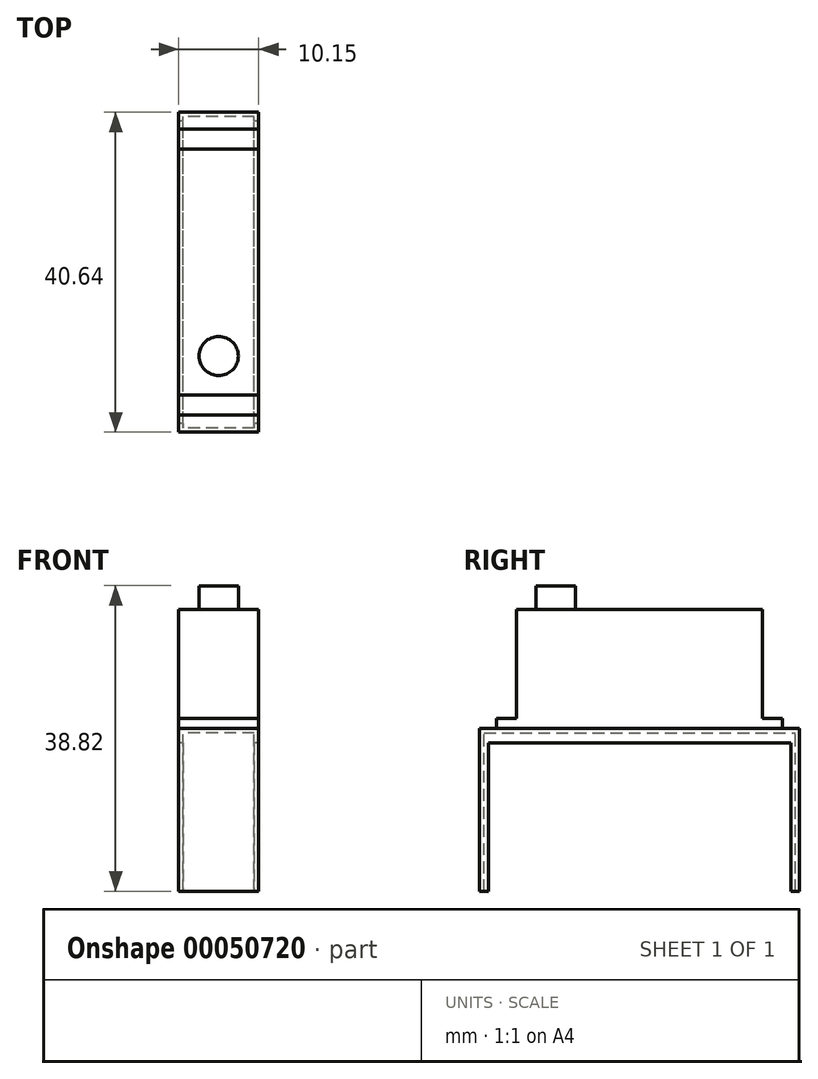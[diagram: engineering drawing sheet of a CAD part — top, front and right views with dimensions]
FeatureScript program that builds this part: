
annotation { "Feature Type Name" : "Feature", "Feature Type Description" : "" }
export const myFeature = defineFeature(function(context is Context, id is Id, definition is map)
    precondition{}
    {
        {
            var Q0;
            Q0=qCreatedBy(makeId("Top.planeOp"),FACE);
            var sketch = newSketch(context, id + "F0", { "sketchPlane" : qUnion([Q0])});
            skLineSegment(sketch, "E0", {"start": v(-5.08, -15.62) * mm, "end": v(-5.08, 15.61) * mm});
            skLineSegment(sketch, "E1", {"start": v(5.07, 15.61) * mm, "end": v(5.07, -15.62) * mm});
            skLineSegment(sketch, "E2", {"start": v(5.07, 15.61) * mm, "end": v(-5.08, 15.61) * mm});
            skLineSegment(sketch, "E3", {"start": v(-5.08, -15.62) * mm, "end": v(5.07, -15.62) * mm});
            skLineSegment(sketch, "E4", {"start": v(-5.08, 15.61) * mm, "end": v(-5.08, 18.17) * mm});
            skLineSegment(sketch, "E5", {"start": v(-5.08, 18.17) * mm, "end": v(5.07, 18.17) * mm});
            skLineSegment(sketch, "E6", {"start": v(5.07, 18.17) * mm, "end": v(5.07, 15.61) * mm});
            skLineSegment(sketch, "E7", {"start": v(-5.08, -15.62) * mm, "end": v(-5.08, -18.16) * mm});
            skLineSegment(sketch, "E8", {"start": v(-5.08, -18.16) * mm, "end": v(5.07, -18.16) * mm});
            skLineSegment(sketch, "E9", {"start": v(5.07, -18.16) * mm, "end": v(5.07, -15.62) * mm});
            skSolve(sketch);
        }
        {
            var Q0;
            Q0=makeQuery(id+"F0.imprint","IMPRINT",FACE,{"disambiguationData":[TD([[makeQuery(id+"F0.imprint","IMPRINT",EDGE,{"derivedFrom":sQuery(id+"F0.wireOp",EDGE,"E0")}),-1.0]])]});
            extrude(context, id + "F1", {"entities" : qUnion([Q0]), "depth" : 15.1 * mm});
        }
        {
            var Q0;
            Q0=makeQuery(id+"F0.imprint","IMPRINT",FACE,{"disambiguationData":[TD([[makeQuery(id+"F0.imprint","IMPRINT",EDGE,{"derivedFrom":sQuery(id+"F0.wireOp",EDGE,"E3")}),-1.0]])]});
            var Q1;
            Q1=makeQuery(id+"F0.imprint","IMPRINT",FACE,{"disambiguationData":[TD([[makeQuery(id+"F0.imprint","IMPRINT",EDGE,{"derivedFrom":sQuery(id+"F0.wireOp",EDGE,"E2")}),-1.0]])]});
            extrude(context, id + "F2", {"entities" : qUnion([Q0, Q1]), "operationType" : NewBodyOperationType.ADD, "depth" : 1.27 * mm});
        }
        {
            var Q0;
            Q0=makeQuery(id+"F1.opExtrude","CAP_FACE",FACE,{"disambiguationData":[OSD([sQuery(id+"F0.wireOp",EDGE,"E0"),sQuery(id+"F0.wireOp",EDGE,"E1"),sQuery(id+"F0.wireOp",EDGE,"E2"),sQuery(id+"F0.wireOp",EDGE,"E3")])],"isStart":false});
            var sketch = newSketch(context, id + "F3", { "sketchPlane" : qUnion([Q0])});
            skCircle(sketch, "E10", {"center": v(0, -10.64) * mm, "radius": 2.49 * mm});
            skSolve(sketch);
        }
        {
            var Q0;
            Q0=makeQuery(id+"F3.imprint","IMPRINT",FACE,{"disambiguationData":[TD([[makeQuery(id+"F3.imprint","IMPRINT",EDGE,{"derivedFrom":sQuery(id+"F3.wireOp",EDGE,"E10")}),1.0]])]});
            extrude(context, id + "F4", {"entities" : qUnion([Q0]), "operationType" : NewBodyOperationType.ADD, "depth" : 3.02 * mm});
        }
        {
            var Q0;
            {var subQ0=sQuery(id+"F0.wireOp",EDGE,"E3");var subQ1=sQuery(id+"F0.wireOp",EDGE,"E2");Q0=makeQuery(id+"F2.boolean.opBoolean","MERGE",FACE,{"derivedFrom":[makeQuery(id+"F1.opExtrude","CAP_FACE",FACE,{"disambiguationData":[OSD([sQuery(id+"F0.wireOp",EDGE,"E0"),sQuery(id+"F0.wireOp",EDGE,"E1"),subQ1,subQ0])],"isStart":true}),makeQuery(id+"F2.opExtrude","CAP_FACE",FACE,{"disambiguationData":[OSD([subQ1,sQuery(id+"F0.wireOp",EDGE,"E4"),sQuery(id+"F0.wireOp",EDGE,"E5"),sQuery(id+"F0.wireOp",EDGE,"E6")])],"isStart":true}),makeQuery(id+"F2.opExtrude","CAP_FACE",FACE,{"disambiguationData":[OSD([subQ0,sQuery(id+"F0.wireOp",EDGE,"E7"),sQuery(id+"F0.wireOp",EDGE,"E8"),sQuery(id+"F0.wireOp",EDGE,"E9")])],"isStart":true})]});}
            var sketch = newSketch(context, id + "F5", { "sketchPlane" : qUnion([Q0])});
            skLineSegment(sketch, "E11", {"start": v(5.07, 20.32) * mm, "end": v(-5.08, 20.32) * mm});
            skLineSegment(sketch, "E12", {"start": v(-5.08, 20.32) * mm, "end": v(-5.08, -20.32) * mm});
            skLineSegment(sketch, "E13", {"start": v(-5.08, -20.32) * mm, "end": v(5.07, -20.32) * mm});
            skLineSegment(sketch, "E14", {"start": v(5.07, -20.32) * mm, "end": v(5.07, 20.32) * mm});
            skLineSegment(sketch, "E15", {"start": v(5.07, -19.77) * mm, "end": v(-5.08, -19.77) * mm});
            skLineSegment(sketch, "E16", {"start": v(5.07, 20.32) * mm, "end": v(5.07, 19.76) * mm});
            skLineSegment(sketch, "E17", {"start": v(5.07, 19.76) * mm, "end": v(-5.08, 19.76) * mm});
            skSolve(sketch);
        }
        {
            var Q0;
            {var subQ2=sQuery(id+"F5.wireOp",EDGE,"E17");Q0=makeQuery(id+"F5.imprint","IMPRINT",FACE,{"disambiguationData":[TD([[makeQuery(id+"F5.imprint","IMPRINT",EDGE,{"derivedFrom":subQ2}),1.0]])]});}
            var Q1;
            {var subQ1=makeQuery(id+"F2.opExtrude","CAP_EDGE",EDGE,{"disambiguationData":[OSD([sQuery(id+"F0.wireOp",EDGE,"E5")])],"isStart":true});Q1=makeQuery(id+"F5.imprint","IMPRINT",FACE,{"disambiguationData":[TD([[makeQuery(id+"F5.imprint","IMPRINT",EDGE,{"derivedFrom":subQ1}),1.0]])]});}
            var Q2;
            {var subQ2=sQuery(id+"F5.wireOp",EDGE,"E15");Q2=makeQuery(id+"F5.imprint","IMPRINT",FACE,{"disambiguationData":[TD([[makeQuery(id+"F5.imprint","IMPRINT",EDGE,{"derivedFrom":subQ2}),-1.0]])]});}
            extrude(context, id + "F6", {"entities" : qUnion([Q0, Q1, Q2]), "depth" : 0.56 * mm});
        }
        {
            var Q0;
            {var subQ0=sQuery(id+"F5.wireOp",EDGE,"E11");Q0=makeQuery(id+"F5.imprint","IMPRINT",FACE,{"disambiguationData":[TD([[makeQuery(id+"F5.imprint","IMPRINT",EDGE,{"derivedFrom":subQ0}),1.0]])]});}
            var Q1;
            {var subQ0=sQuery(id+"F5.wireOp",EDGE,"E13");Q1=makeQuery(id+"F5.imprint","IMPRINT",FACE,{"disambiguationData":[TD([[makeQuery(id+"F5.imprint","IMPRINT",EDGE,{"derivedFrom":subQ0}),1.0]])]});}
            extrude(context, id + "F7", {"entities" : qUnion([Q0, Q1]), "operationType" : NewBodyOperationType.ADD, "depth" : 20.68 * mm});
        }
        {
            var Q0;
            Q0=makeQuery(id+"F6.opExtrude","CAP_FACE",FACE,{"disambiguationData":[OSD([sQuery(id+"F5.wireOp",EDGE,"E12"),sQuery(id+"F5.wireOp",EDGE,"E14"),sQuery(id+"F5.wireOp",EDGE,"E15"),sQuery(id+"F5.wireOp",EDGE,"E17")])],"isStart":false});
            var sketch = newSketch(context, id + "F8", { "sketchPlane" : qUnion([Q0])});
            skLineSegment(sketch, "E18", {"start": v(5.07, 19.76) * mm, "end": v(4.51, 19.76) * mm});
            skLineSegment(sketch, "E19", {"start": v(4.51, 19.76) * mm, "end": v(4.51, -19.77) * mm});
            skLineSegment(sketch, "E20", {"start": v(4.51, -19.77) * mm, "end": v(5.07, -19.77) * mm});
            skLineSegment(sketch, "E21", {"start": v(5.07, -19.77) * mm, "end": v(5.07, 19.76) * mm});
            skLineSegment(sketch, "E22", {"start": v(-5.08, 19.76) * mm, "end": v(-4.53, 19.76) * mm});
            skLineSegment(sketch, "E23", {"start": v(-4.53, 19.76) * mm, "end": v(-4.53, -19.77) * mm});
            skLineSegment(sketch, "E24", {"start": v(-4.53, -19.77) * mm, "end": v(-5.08, -19.77) * mm});
            skLineSegment(sketch, "E25", {"start": v(-5.08, -19.77) * mm, "end": v(-5.08, 19.76) * mm});
            skSolve(sketch);
        }
        {
            var Q0;
            Q0 = qSketchRegion(id + "F8", true);
            extrude(context, id + "F9", {"entities" : qUnion([Q0]), "operationType" : NewBodyOperationType.ADD, "depth" : 1.27 * mm});
        }
        {
            var Q0;
            Q0=makeQuery(id+"F7.opExtrude","SWEPT_FACE",FACE,{"disambiguationData":[OSD([sQuery(id+"F5.wireOp",EDGE,"E17")])]});
            var sketch = newSketch(context, id + "F10", { "sketchPlane" : qUnion([Q0])});
            skLineSegment(sketch, "E26", {"start": v(5.08, -1.83) * mm, "end": v(4.53, -1.83) * mm});
            skLineSegment(sketch, "E27", {"start": v(4.53, -1.83) * mm, "end": v(4.53, -20.68) * mm});
            skLineSegment(sketch, "E28", {"start": v(4.53, -20.68) * mm, "end": v(5.08, -20.68) * mm});
            skLineSegment(sketch, "E29", {"start": v(5.08, -20.68) * mm, "end": v(5.08, -1.83) * mm});
            skLineSegment(sketch, "E30", {"start": v(-5.07, -1.83) * mm, "end": v(-4.51, -1.83) * mm});
            skLineSegment(sketch, "E31", {"start": v(-4.51, -1.83) * mm, "end": v(-4.51, -20.68) * mm});
            skLineSegment(sketch, "E32", {"start": v(-4.51, -20.68) * mm, "end": v(-5.07, -20.68) * mm});
            skLineSegment(sketch, "E33", {"start": v(-5.07, -20.68) * mm, "end": v(-5.07, -1.83) * mm});
            skSolve(sketch);
        }
        {
            var Q0;
            Q0 = qSketchRegion(id + "F10", true);
            extrude(context, id + "F11", {"entities" : qUnion([Q0]), "operationType" : NewBodyOperationType.ADD, "depth" : 0.56 * mm});
        }
        {
            var Q0;
            Q0=makeQuery(id+"F7.opExtrude","SWEPT_FACE",FACE,{"disambiguationData":[OSD([sQuery(id+"F5.wireOp",EDGE,"E15")])]});
            var sketch = newSketch(context, id + "F12", { "sketchPlane" : qUnion([Q0])});
            skLineSegment(sketch, "E34", {"start": v(-5.08, -1.83) * mm, "end": v(-4.53, -1.83) * mm});
            skLineSegment(sketch, "E35", {"start": v(-4.53, -1.83) * mm, "end": v(-4.53, -20.68) * mm});
            skLineSegment(sketch, "E36", {"start": v(-4.53, -20.68) * mm, "end": v(-5.08, -20.68) * mm});
            skLineSegment(sketch, "E37", {"start": v(-5.08, -20.68) * mm, "end": v(-5.08, -1.83) * mm});
            skLineSegment(sketch, "E38", {"start": v(5.07, -1.83) * mm, "end": v(4.51, -1.83) * mm});
            skLineSegment(sketch, "E39", {"start": v(4.51, -1.83) * mm, "end": v(4.51, -20.68) * mm});
            skLineSegment(sketch, "E40", {"start": v(4.51, -20.68) * mm, "end": v(5.07, -20.68) * mm});
            skLineSegment(sketch, "E41", {"start": v(5.07, -20.68) * mm, "end": v(5.07, -1.83) * mm});
            skSolve(sketch);
        }
        {
            var Q0;
            Q0 = qSketchRegion(id + "F12", true);
            extrude(context, id + "F13", {"entities" : qUnion([Q0]), "operationType" : NewBodyOperationType.ADD, "depth" : 0.56 * mm});
        }
    });
